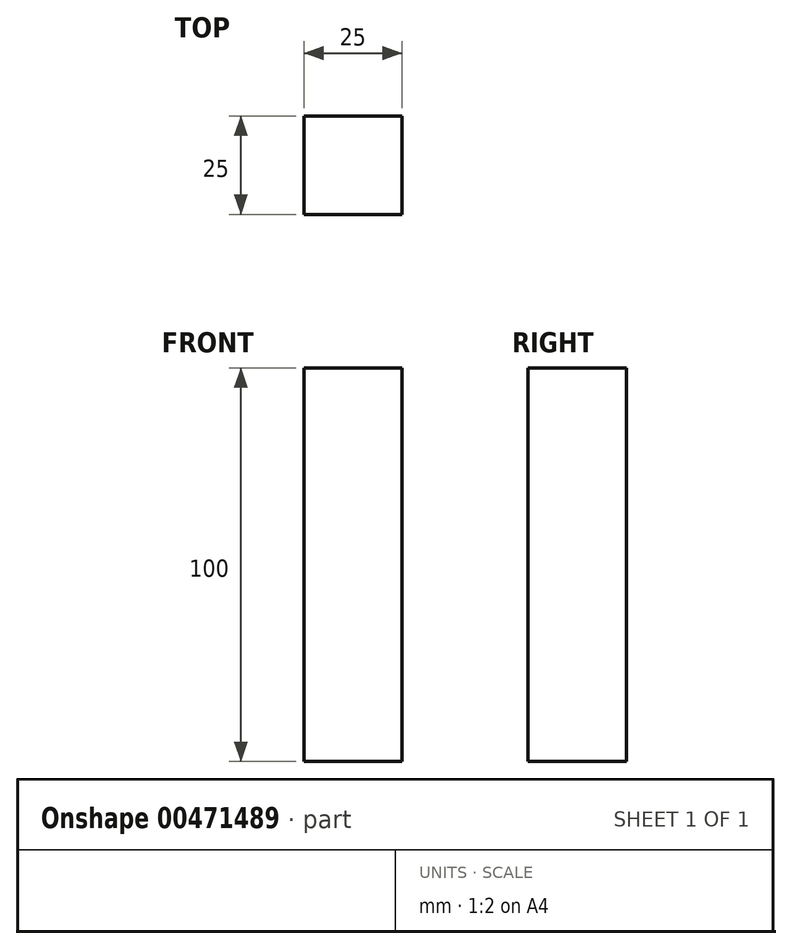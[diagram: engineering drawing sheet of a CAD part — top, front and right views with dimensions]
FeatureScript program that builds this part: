
annotation { "Feature Type Name" : "Feature", "Feature Type Description" : "" }
export const myFeature = defineFeature(function(context is Context, id is Id, definition is map)
    precondition{}
    {
        {
            var Q0;
            Q0=qCreatedBy(makeId("Top.planeOp"),FACE);
            var sketch = newSketch(context, id + "F0", { "sketchPlane" : qUnion([Q0])});
            skLineSegment(sketch, "E0.bottom", {"start": v(12.5, 12.5) * mm, "end": v(-12.5, 12.5) * mm});
            skLineSegment(sketch, "E0.top", {"start": v(12.5, -12.5) * mm, "end": v(-12.5, -12.5) * mm});
            skLineSegment(sketch, "E0.left", {"start": v(12.5, 12.5) * mm, "end": v(12.5, -12.5) * mm});
            skLineSegment(sketch, "E0.right", {"start": v(-12.5, 12.5) * mm, "end": v(-12.5, -12.5) * mm});
            skPoint(sketch, "E0.middle", {"position": v(0, 0) * mm});
            skSolve(sketch);
        }
        {
            var Q0;
            Q0 = qSketchRegion(id + "F0", true);
            extrude(context, id + "F1", {"entities" : qUnion([Q0]), "depth" : 100 * mm});
        }
    });
